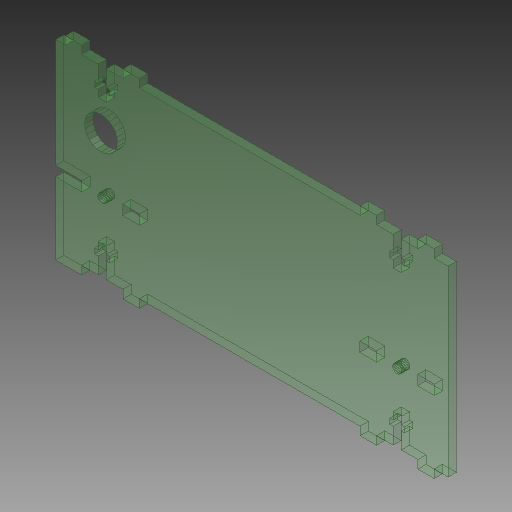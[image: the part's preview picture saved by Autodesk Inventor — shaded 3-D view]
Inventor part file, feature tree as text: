
AUTODESK INVENTOR PART (.ipt)
format: ipt  version: 2018 (Build 220112000, 112)  size: 290,304 bytes
history: native  units: mm
features: extrude x1, sketch x1
ambient origin geometry x8: Origin, YZ Plane, XZ Plane, XY Plane, X Axis, Y Axis, Z Axis, Center Point
bodies: Solid1 (feature_tree)
feature tree (2):
  extrude  "Extrusion1"  [1 undecoded]
  sketch  "Sketch1"  dims[d0=3.0mm d1=0.0mm]
note: 1 required parameter value undecoded (feature->parameter linkage not recoverable at this tier; creation-order binding heuristic only, values carry confidence <= 0.55)
